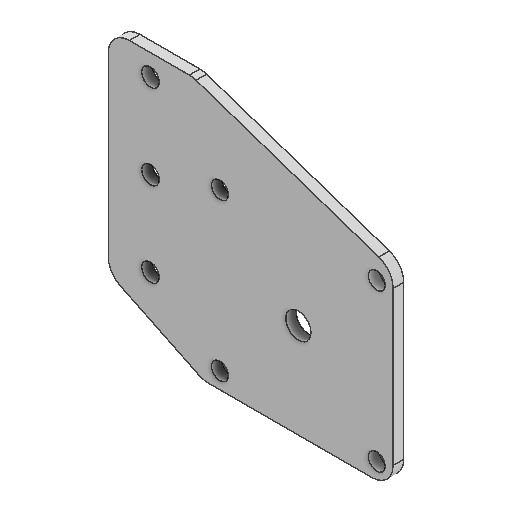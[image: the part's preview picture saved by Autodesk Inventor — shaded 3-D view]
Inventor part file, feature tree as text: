
AUTODESK INVENTOR PART (.ipt)
format: ipt  version: 2025.2 (Build 292293000, 293)  size: 153,600 bytes
history: native  units: in
note: dims shown in document units (in); Inventor stores cm internally (conversion verified against a paired STEP export)
features: extrude x1, fillet x1, sketch x1
ambient origin geometry x8: Origin, YZ Plane, XZ Plane, XY Plane, X Axis, Y Axis, Z Axis, Center Point
bodies: Solid1 (feature_tree)
feature tree (3):
  extrude  "Extrusion1"  Depth=0.25in
  fillet  "Fillet1"  Radius=0.201in
  sketch  "Sketch1"  dims[d0=2.244in d1=2.244in d3=0.201in d4=0.201in d5=0.201in d7=0.201in d15=1.122in d16=1.122in d17=2.5in d18=1.0in d19=1.0in d20=0.0in d21=0.209in d22=0.209in d23=0.209in d24=1.125in d26=0.5in d28=0.0in d29=0.0in d30=0.5in d33=3.3in d34=1.75in d35=0.125in d36=0.0in d37=0.3in d38=0.25in d39=2.6247in d40=2.6247in d41=1.3123in d42=1.3123in]
